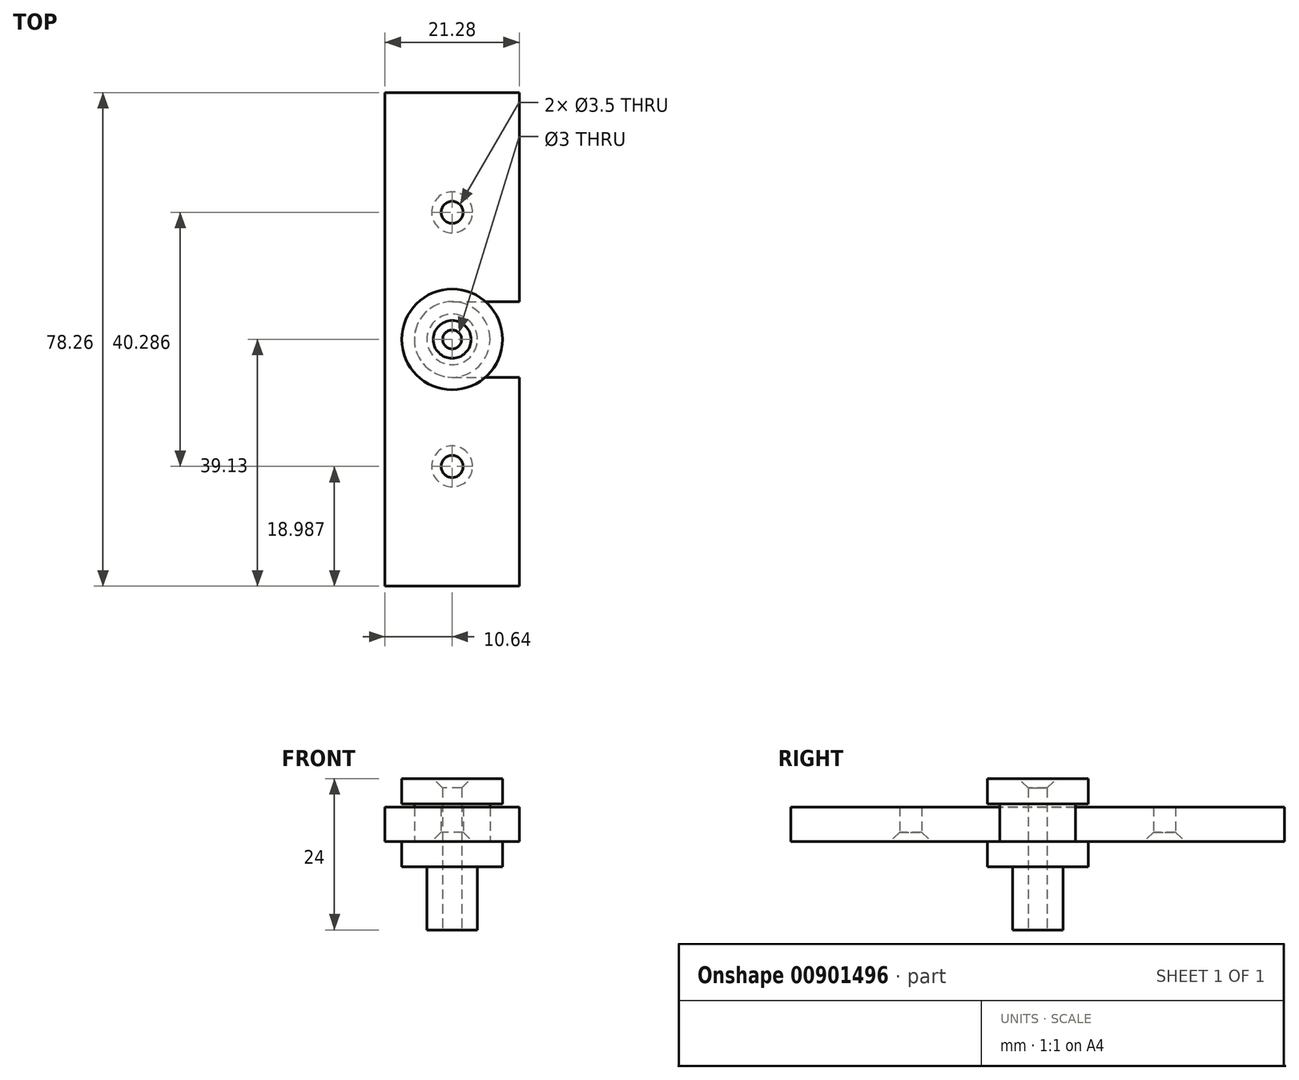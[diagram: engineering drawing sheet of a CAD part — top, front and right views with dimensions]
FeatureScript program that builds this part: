
annotation { "Feature Type Name" : "Feature", "Feature Type Description" : "" }
export const myFeature = defineFeature(function(context is Context, id is Id, definition is map)
    precondition{}
    {
        {
            var Q0;
            Q0=qCreatedBy(makeId("Top.planeOp"),FACE);
            var sketch = newSketch(context, id + "F0", { "sketchPlane" : qUnion([Q0])});
            skCircle(sketch, "E0", {"center": v(0, 0) * mm, "radius": 4 * mm});
            skCircle(sketch, "E1", {"center": v(0, 0) * mm, "radius": 1.5 * mm});
            skSolve(sketch);
        }
        {
            var Q0;
            Q0=makeQuery(id+"F0.imprint","IMPRINT",FACE,{"disambiguationData":[TD([[makeQuery(id+"F0.imprint","IMPRINT",EDGE,{"derivedFrom":sQuery(id+"F0.wireOp",EDGE,"E0")}),1.0]])]});
            var Q1;
            Q1=makeQuery(id+"F0.imprint","IMPRINT",FACE,{"disambiguationData":[TD([[makeQuery(id+"F0.imprint","IMPRINT",EDGE,{"derivedFrom":sQuery(id+"F0.wireOp",EDGE,"E1")}),1.0]])]});
            extrude(context, id + "F1", {"entities" : qUnion([Q0, Q1]), "depth" : 10 * mm, "offsetDistance" : 25 * mm});
        }
        {
            var Q0;
            Q0=makeQuery(id+"F1.opExtrude","CAP_FACE",FACE,{"disambiguationData":[OSD([sQuery(id+"F0.wireOp",EDGE,"E0"),sQuery(id+"F0.wireOp",EDGE,"E1")])],"isStart":false});
            var sketch = newSketch(context, id + "F2", { "sketchPlane" : qUnion([Q0])});
            skCircle(sketch, "E2", {"center": v(0, 0) * mm, "radius": 8 * mm});
            skSolve(sketch);
        }
        {
            var Q0;
            Q0=qSketchRegion(id+"F2",true);
            extrude(context, id + "F3", {"entities" : qUnion([Q0]), "operationType" : NewBodyOperationType.ADD, "depth" : 4 * mm, "offsetDistance" : 25 * mm});
        }
        {
            var Q0;
            Q0=makeQuery(id+"F3.opExtrude","CAP_FACE",FACE,{"disambiguationData":[OSD([sQuery(id+"F2.wireOp",EDGE,"E2")])],"isStart":false});
            var sketch = newSketch(context, id + "F4", { "sketchPlane" : qUnion([Q0])});
            skCircle(sketch, "E3", {"center": v(0, 0) * mm, "radius": 6 * mm});
            skSolve(sketch);
        }
        {
            var Q0;
            Q0=makeQuery(id+"F4.imprint","IMPRINT",FACE,{"disambiguationData":[TD([[makeQuery(id+"F4.imprint","IMPRINT",EDGE,{"derivedFrom":sQuery(id+"F4.wireOp",EDGE,"E3")}),1.0]])]});
            extrude(context, id + "F5", {"entities" : qUnion([Q0]), "operationType" : NewBodyOperationType.ADD, "depth" : 6 * mm, "offsetDistance" : 25 * mm});
        }
        {
            var Q0;
            Q0=makeQuery(id+"F5.opExtrude","CAP_FACE",FACE,{"disambiguationData":[OSD([sQuery(id+"F4.wireOp",EDGE,"E3")])],"isStart":false});
            var sketch = newSketch(context, id + "F6", { "sketchPlane" : qUnion([Q0])});
            skCircle(sketch, "E4", {"center": v(0, 0) * mm, "radius": 8 * mm});
            skSolve(sketch);
        }
        {
            var Q0;
            Q0=qSketchRegion(id+"F6",true);
            extrude(context, id + "F7", {"entities" : qUnion([Q0]), "operationType" : NewBodyOperationType.ADD, "depth" : 4 * mm, "offsetDistance" : 25 * mm});
        }
        {
            var Q0;
            Q0=makeQuery(id+"F0.imprint","IMPRINT",FACE,{"disambiguationData":[TD([[makeQuery(id+"F0.imprint","IMPRINT",EDGE,{"derivedFrom":sQuery(id+"F0.wireOp",EDGE,"E1")}),1.0]])]});
            extrude(context, id + "F8", {"entities" : qUnion([Q0]), "operationType" : NewBodyOperationType.REMOVE, "endBound" : BoundingType.THROUGH_ALL, "depth" : 25 * mm, "offsetDistance" : 25 * mm});
        }
        {
            var Q0;
            Q0=makeQuery(id+"F8.boolean.opBoolean","INTERSECT",EDGE,{"derivedFrom":[makeQuery(id+"F7.opExtrude","CAP_FACE",FACE,{"disambiguationData":[OSD([sQuery(id+"F6.wireOp",EDGE,"E4")])],"isStart":false}),makeQuery(id+"F8.opExtrude","SWEPT_FACE",FACE,{"disambiguationData":[OSD([sQuery(id+"F0.wireOp",EDGE,"E1")])]})]});
            chamfer(context, id + "F9", {"entities" : qUnion([Q0]), "width" : 1.5 * mm, "tangentPropagation" : true});
        }
        {
            var Q0;
            Q0=makeQuery(id+"F3.opExtrude","CAP_FACE",FACE,{"disambiguationData":[OSD([sQuery(id+"F2.wireOp",EDGE,"E2")])],"isStart":false});
            var sketch = newSketch(context, id + "F10", { "sketchPlane" : qUnion([Q0])});
            skLineSegment(sketch, "E5.bottom", {"start": v(-10.64, -39.13) * mm, "end": v(10.64, -39.13) * mm});
            skLineSegment(sketch, "E5.top", {"start": v(-10.64, 39.13) * mm, "end": v(10.64, 39.13) * mm});
            skLineSegment(sketch, "E5.left", {"start": v(-10.64, -39.13) * mm, "end": v(-10.64, 39.13) * mm});
            skLineSegment(sketch, "E5.right", {"start": v(10.64, -39.13) * mm, "end": v(10.64, 39.13) * mm});
            skPoint(sketch, "E5.middle", {"position": v(0, 0) * mm});
            skCircle(sketch, "E6.0", {"center": v(0, 0) * mm, "radius": 6 * mm});
            skCircle(sketch, "E7.0", {"center": v(0, 0) * mm, "radius": 8 * mm});
            skLineSegment(sketch, "E8", {"start": v(0, 6) * mm, "end": v(10.64, 6) * mm});
            skLineSegment(sketch, "E9", {"start": v(0, -6) * mm, "end": v(10.64, -6) * mm});
            skLineSegment(sketch, "E10", {"start": v(0, 39.13) * mm, "end": v(0, -39.13) * mm, "construction": true});
            skCircle(sketch, "E11", {"center": v(0, 20.14) * mm, "radius": 1.75 * mm});
            skLineSegment(sketch, "E12", {"start": v(-10.64, 0) * mm, "end": v(10.64, 0) * mm, "construction": true});
            skCircle(sketch, "E13.MirrorC", {"center": v(0, -20.14) * mm, "radius": 1.75 * mm});
            skSolve(sketch);
        }
        {
            var Q0;
            {var subQ1=sQuery(id+"F10.wireOp",EDGE,"E5.bottom");Q0=makeQuery(id+"F10.imprint","IMPRINT",FACE,{"disambiguationData":[TD([[makeQuery(id+"F10.imprint","IMPRINT",EDGE,{"derivedFrom":subQ1}),1.0]])]});}
            var Q1;
            {var subQ0=sQuery(id+"F10.wireOp",EDGE,"E8");var subQ1=sQuery(id+"F10.wireOp",EDGE,"E6.0");var subQ2=makeQuery(id+"F10.imprint","INTERSECT",VERTEX,{"derivedFrom":[subQ1,subQ0]});Q1=makeQuery(id+"F10.imprint","IMPRINT",FACE,{"disambiguationData":[TD([[makeQuery(id+"F10.imprint","IMPRINT",EDGE,{"disambiguationData":[TD([[subQ2,-1.0]])],"derivedFrom":subQ1}),-1.0]])]});}
            extrude(context, id + "F11", {"entities" : qUnion([Q0, Q1]), "depth" : 5.5 * mm, "offsetDistance" : 25 * mm});
        }
        {
            var Q0;
            Q0=makeQuery(id+"F11.opExtrude","CAP_EDGE",EDGE,{"disambiguationData":[OSD([sQuery(id+"F10.wireOp",EDGE,"E11")])],"isStart":true});
            var Q1;
            Q1=makeQuery(id+"F11.opExtrude","CAP_EDGE",EDGE,{"disambiguationData":[OSD([sQuery(id+"F10.wireOp",EDGE,"E13.MirrorC")])],"isStart":true});
            chamfer(context, id + "F12", {"entities" : qUnion([Q0, Q1]), "width" : 1.5 * mm, "tangentPropagation" : true});
        }
    });
